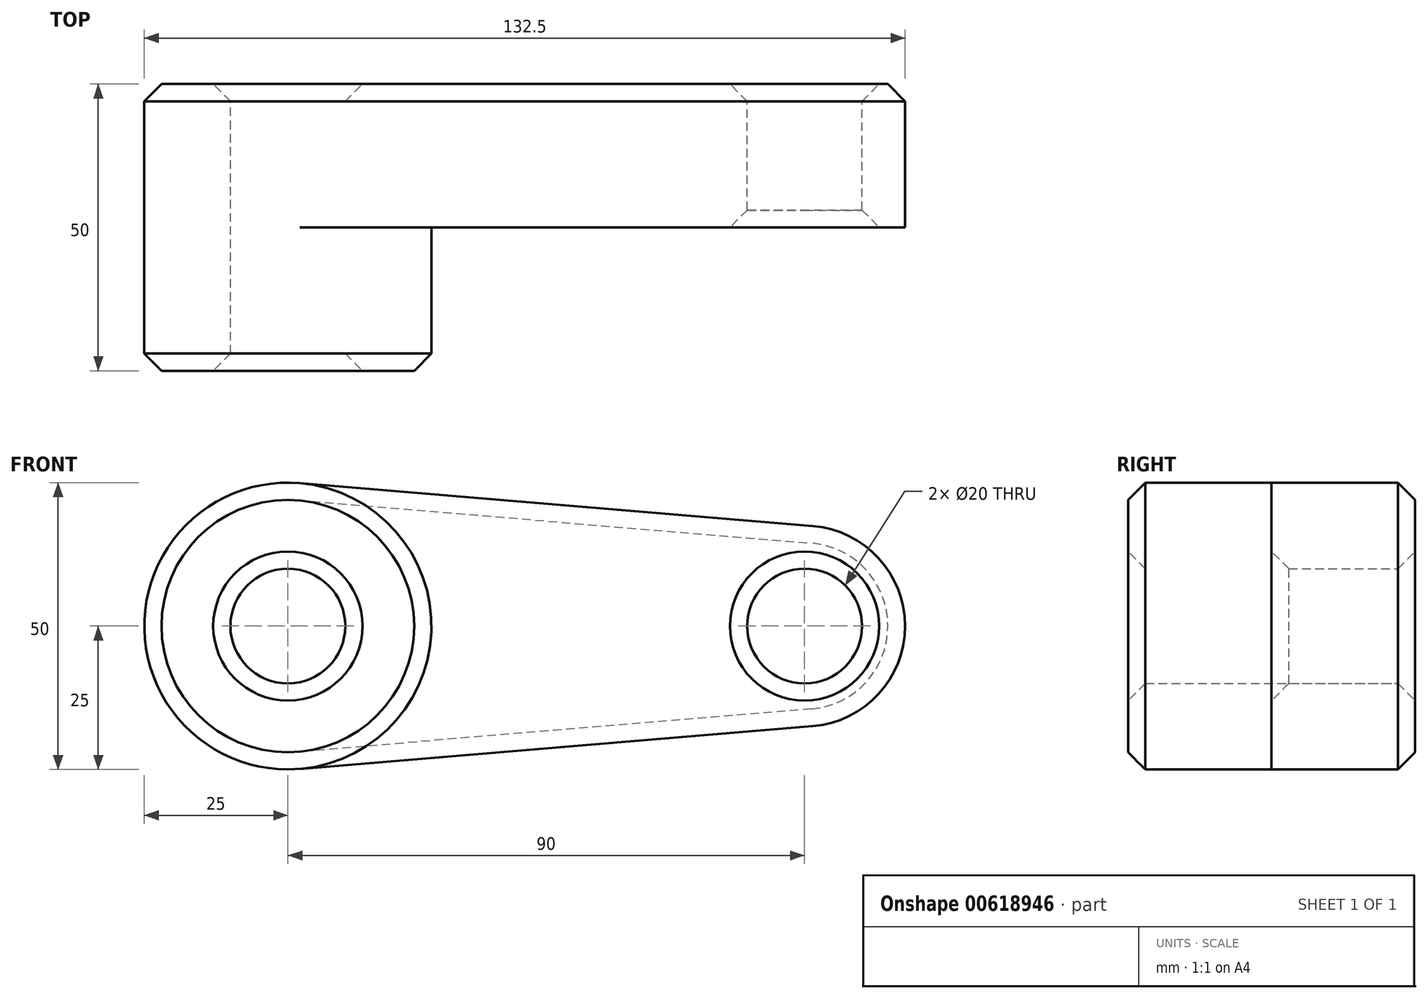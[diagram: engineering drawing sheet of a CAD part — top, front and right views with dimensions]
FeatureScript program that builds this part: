
annotation { "Feature Type Name" : "Feature", "Feature Type Description" : "" }
export const myFeature = defineFeature(function(context is Context, id is Id, definition is map)
    precondition{}
    {
        {
            var Q0;
            Q0=qCreatedBy(makeId("Front.planeOp"),FACE);
            var sketch = newSketch(context, id + "F0", { "sketchPlane" : qUnion([Q0])});
            skCircle(sketch, "E0", {"center": v(0, 0) * mm, "radius": 25 * mm});
            skCircle(sketch, "E1", {"center": v(90, 0) * mm, "radius": 17.5 * mm});
            skLineSegment(sketch, "E2", {"start": v(2.08, 24.91) * mm, "end": v(91.46, 17.44) * mm});
            skLineSegment(sketch, "E3", {"start": v(2.08, -24.91) * mm, "end": v(91.46, -17.44) * mm});
            skCircle(sketch, "E4", {"center": v(0, 0) * mm, "radius": 10 * mm});
            skCircle(sketch, "E5", {"center": v(90, 0) * mm, "radius": 10 * mm});
            skSolve(sketch);
        }
        {
            var Q0;
            Q0=qSketchRegion(id+"F0",true);
            extrude(context, id + "F1", {"entities" : qUnion([Q0]), "depth" : 25 * mm});
        }
        {
            var Q0;
            Q0=makeQuery(id+"F0.imprint","IMPRINT",FACE,{"disambiguationData":[TD([[makeQuery(id+"F0.imprint","IMPRINT",EDGE,{"derivedFrom":sQuery(id+"F0.wireOp",EDGE,"E4")}),-1.0]])]});
            extrude(context, id + "F2", {"entities" : qUnion([Q0]), "operationType" : NewBodyOperationType.ADD, "depth" : 50 * mm});
        }
        {
            var Q0;
            Q0=makeQuery(id+"F2.opExtrude","CAP_EDGE",EDGE,{"disambiguationData":[OSD([sQuery(id+"F0.wireOp",EDGE,"E0")])],"isStart":false});
            var Q1;
            Q1=makeQuery(id+"F2.opExtrude","CAP_EDGE",EDGE,{"disambiguationData":[OSD([sQuery(id+"F0.wireOp",EDGE,"E4")])],"isStart":false});
            var Q2;
            Q2=makeQuery(id+"F1.opExtrude","CAP_EDGE",EDGE,{"disambiguationData":[OSD([sQuery(id+"F0.wireOp",EDGE,"E5")])],"isStart":false});
            chamfer(context, id + "F3", {"entities" : qUnion([Q0, Q1, Q2]), "width" : 3 * mm, "tangentPropagation" : true});
        }
        {
            var Q0;
            Q0=makeQuery(id+"F1.opExtrude","CAP_EDGE",EDGE,{"disambiguationData":[OSD([sQuery(id+"F0.wireOp",EDGE,"E5")])],"isStart":true});
            var Q1;
            Q1=makeQuery(id+"F1.opExtrude","CAP_EDGE",EDGE,{"disambiguationData":[OSD([sQuery(id+"F0.wireOp",EDGE,"E4")])],"isStart":true});
            var Q2;
            Q2=makeQuery(id+"F1.opExtrude","CAP_EDGE",EDGE,{"disambiguationData":[OSD([sQuery(id+"F0.wireOp",EDGE,"E0")])],"isStart":true});
            var Q3;
            Q3=makeQuery(id+"F1.opExtrude","CAP_EDGE",EDGE,{"disambiguationData":[OSD([sQuery(id+"F0.wireOp",EDGE,"E3")])],"isStart":true});
            var Q4;
            Q4=makeQuery(id+"F1.opExtrude","CAP_EDGE",EDGE,{"disambiguationData":[OSD([sQuery(id+"F0.wireOp",EDGE,"E2")])],"isStart":true});
            var Q5;
            Q5=makeQuery(id+"F1.opExtrude","CAP_EDGE",EDGE,{"disambiguationData":[OSD([sQuery(id+"F0.wireOp",EDGE,"E1")])],"isStart":true});
            chamfer(context, id + "F4", {"entities" : qUnion([Q0, Q1, Q2, Q3, Q4, Q5]), "width" : 3 * mm, "tangentPropagation" : true});
        }
    });
